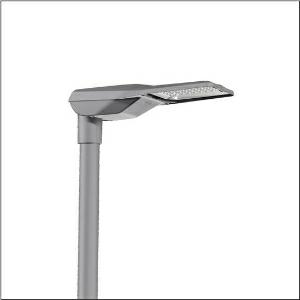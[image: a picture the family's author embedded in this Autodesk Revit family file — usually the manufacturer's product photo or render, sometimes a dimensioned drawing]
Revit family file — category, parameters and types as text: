
# Revit family: streetlight_sl_21_iq_mini___p0_8a_5xe2u31g08hb_4850
name_source: partatom
category: Lighting Fixtures
units: mm (PartAtom-declared; Revit-internal decimal feet)

## family parameters
Cut with Voids When Loaded = No
Host = Face
Light Source = No
Part Type = Normal
Room Calculation Point = No
Round Connector Dimension = Use Diameter
Shared = No

## types (1)
- --- (1 x LED, 9540 lm, 70.9 W, 3000K)
    Apparent Load = 71 VA
    CIE Flux Codes = 33 69 96 100 100
    Color Rendering = 70
    Color Temperature = 3000K
    Default Elevation = 1800 mm
    Description = Streetlight SL 21 iQ mini, mast luminaire, primary light control with lens, of PMMA, primary optical cover: cover, of toughened safety glass, transparent, light distribution: P0.8a, light emission: direct distribution, primary light characteristic: asymmetric, installation type: post-top, side-entry, LED, High Power LED, rated luminous flux: 9.540lm, luminous efficacy: 135lm/W, light colour: 730, colour temperature: 3000K, control gear: iQ Street-Remote, control: pre-setting: linear dimming characteristic, Street-Remote, Auto-Match, Temp-Guard, Lumen-Switch, Night-Set, Smart-Wire, Light-Fading, Desk-Remote (wireless, voltage-free reading and setting of iQ features in the workshop via application-optimized NFC function/RFID function), optimised constant luminous flux control (CLO 2.0), mains connection: 220..240V, AC, 50/60Hz, start of lifetime: 71W, end of service life: 75W, reduction: 31W, luminaire housing, of diecast aluminium, powder-coated, Siteco® metallic grey (DB 702S), corrosivity category C5 mid according to DIN EN ISO 12944, please order mast flange separately, inclination adjustable: 0°, 5°, 10°, 15°, sealing non-destructively replaceable, multi-level sealing system, length: 628mm, width: 235mm, height: 110mm, mast flange for spigot size: 42mm (side-entry): 5XC10008XM4, 60/48mm (side-entry/post-top): 5XC10108XM2, 76/60mm (side-entry/post-top): 5XC10108XM1, mounting height: 4..8m, protection rating (complete): IP66, insulation class (complete): insulation class II (safety insulation), certification: CE, ENEC, ENEC+, VDE, impact resistance: IK09, permissible operating ambient temperature for outdoor applications: -40..+50°C, standard-compliant lighting for roads and squares, packaging unit: 1 piece

Light Distribution: P0.8a
    Height = 110 mm
    Lamp = 1 x LED
    Lamp Light Flux = 9540 lm
    Lamp Power = 70.9 W
    Lamp count = 1
    Length = 625 mm
    Luminous efficacy = 135 lm/W
    Manufacturer = Siteco
    ModVariant = No
    Model = 5XE2U31G08HB
    Number of Poles = 1
    OnlyDefault = Yes
    Power Factor = 1
    Product Name = Streetlight SL 21 iQ mini | P0.8a
    Product group = mast luminaire | pylon top
    ProductGroupID = 6100
    Protection Class = Protection class II
    Protection Degree = IP 66
    RLX_Detail_Level = 1
    RLX_Emergency_Light_Flux = 0 lm
    RLX_Emergency_Type = 0
    RLX_Emergency_Type_DB = No
    RlxData = <blob elided: 92041 chars, md5=a851c130>
    Socket = socket
    Standby Power = 0 W
    System Light Flux = 9540 lm
    System Power = 71 W
    Type Comments = factory setting: luminous flux: 100 % | dim-lin: 254 | 711 mA
    Type Image = l_1003519.jpg
    URL = http://relux.com
    VarID = @adj_069370
    Voltage = 0 V
    Weight = 0.00 kg
    Width = 234 mm

## geometry (parser evidence)
native form markers: Blend x4, Sweep x12
no freeform markers — native parametric forms only
